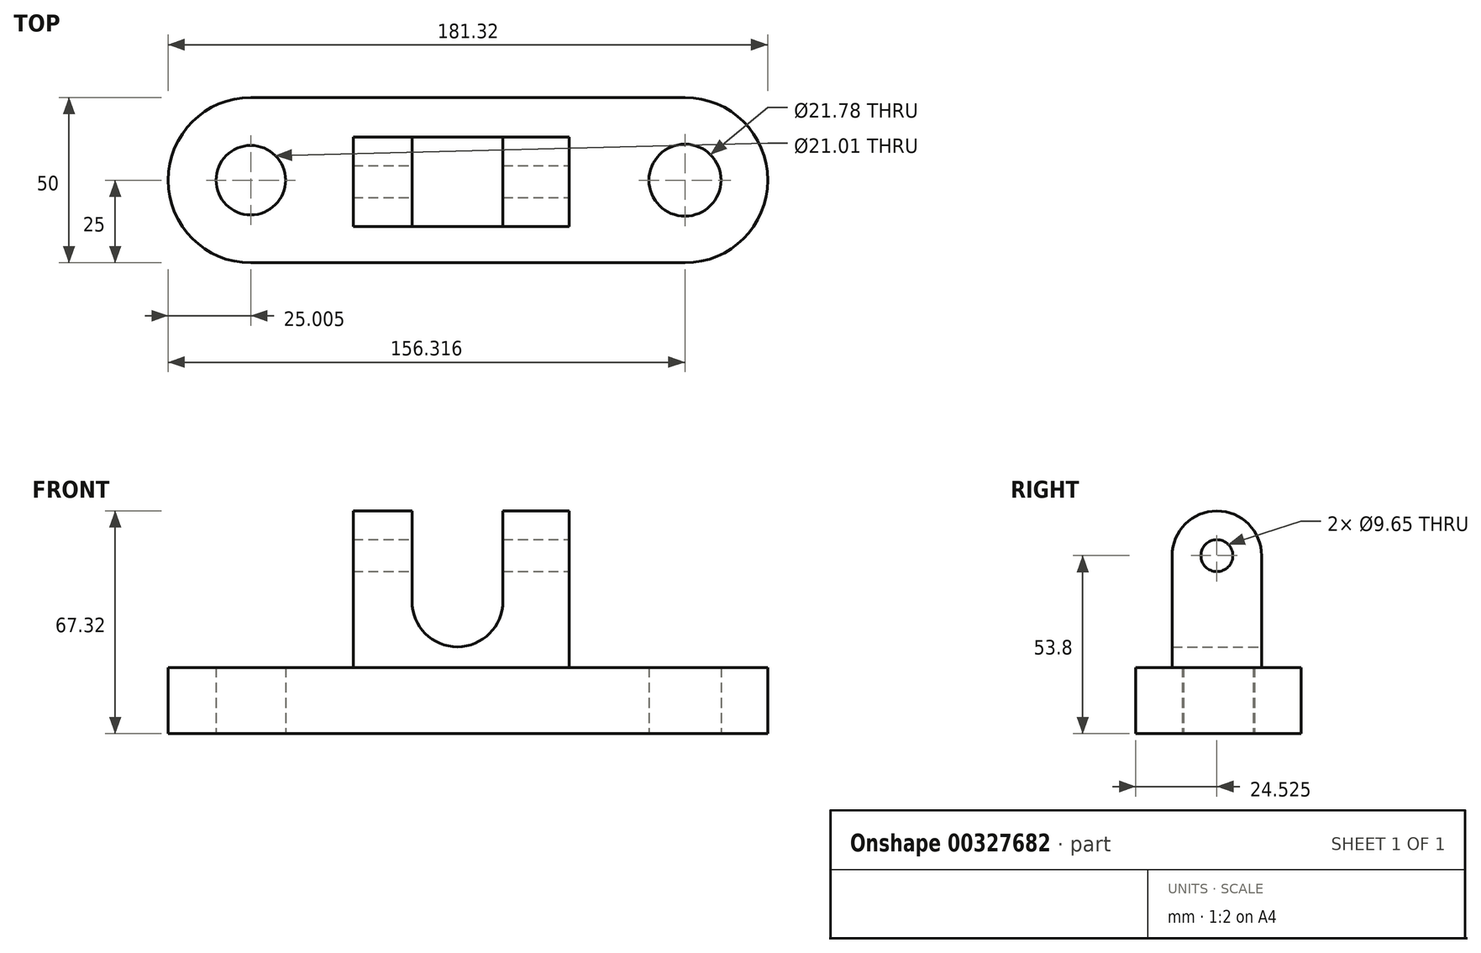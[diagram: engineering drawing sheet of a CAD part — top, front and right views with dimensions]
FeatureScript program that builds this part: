
annotation { "Feature Type Name" : "Feature", "Feature Type Description" : "" }
export const myFeature = defineFeature(function(context is Context, id is Id, definition is map)
    precondition{}
    {
        {
            var Q0;
            Q0=qCreatedBy(makeId("Top.planeOp"),FACE);
            var sketch = newSketch(context, id + "F0", { "sketchPlane" : qUnion([Q0])});
            skLineSegment(sketch, "E0", {"start": v(-77.75, 0) * mm, "end": v(53.57, 0) * mm});
            skArc(sketch, "E1.0.startCap", {"start": v(-77.75, -25) * mm, "mid": v(-102.75, 0) * mm, "end": v(-77.75, 25) * mm});
            skArc(sketch, "E1.0.endCap", {"start": v(53.57, 25) * mm, "mid": v(78.57, 0) * mm, "end": v(53.57, -25) * mm});
            skLineSegment(sketch, "E1.0.left", {"start": v(-77.75, 25) * mm, "end": v(53.57, 25) * mm});
            skLineSegment(sketch, "E1.0.right", {"start": v(-77.75, -25) * mm, "end": v(53.57, -25) * mm});
            skCircle(sketch, "E2", {"center": v(-77.75, 0) * mm, "radius": 10.5 * mm});
            skCircle(sketch, "E3", {"center": v(53.57, 0) * mm, "radius": 10.9 * mm});
            skSolve(sketch);
        }
        {
            var Q0;
            Q0 = qSketchRegion(id + "F0", true);
            extrude(context, id + "F1", {"entities" : qUnion([Q0]), "depth" : 20 * mm});
        }
        {
            var Q0;
            Q0=makeQuery(id+"F1.opExtrude","CAP_FACE",FACE,{"disambiguationData":[OSD([sQuery(id+"F0.wireOp",EDGE,"E1.0.startCap"),sQuery(id+"F0.wireOp",EDGE,"E1.0.endCap"),sQuery(id+"F0.wireOp",EDGE,"E1.0.left"),sQuery(id+"F0.wireOp",EDGE,"E1.0.right"),sQuery(id+"F0.wireOp",EDGE,"E2"),sQuery(id+"F0.wireOp",EDGE,"E3")])],"isStart":false});
            var sketch = newSketch(context, id + "F2", { "sketchPlane" : qUnion([Q0])});
            skLineSegment(sketch, "E4.bottom", {"start": v(18.48, -14) * mm, "end": v(-46.79, -14) * mm});
            skLineSegment(sketch, "E4.top", {"start": v(18.48, 13.04) * mm, "end": v(-46.79, 13.04) * mm});
            skLineSegment(sketch, "E4.left", {"start": v(18.48, -14) * mm, "end": v(18.48, 13.04) * mm});
            skLineSegment(sketch, "E4.right", {"start": v(-46.79, -14) * mm, "end": v(-46.79, 13.04) * mm});
            skSolve(sketch);
        }
        {
            var Q0;
            Q0 = qSketchRegion(id + "F2", true);
            extrude(context, id + "F3", {"entities" : qUnion([Q0]), "operationType" : NewBodyOperationType.ADD, "depth" : 33.8 * mm});
        }
        {
            var Q0;
            Q0=makeQuery(id+"F3.opExtrude","SWEPT_FACE",FACE,{"disambiguationData":[OSD([sQuery(id+"F2.wireOp",EDGE,"E4.left")])]});
            var sketch = newSketch(context, id + "F4", { "sketchPlane" : qUnion([Q0])});
            skArc(sketch, "E5", {"start": v(13.04, 53.8) * mm, "mid": v(-0.48, 67.32) * mm, "end": v(-14, 53.8) * mm});
            skLineSegment(sketch, "E6", {"start": v(-14, 53.8) * mm, "end": v(13.04, 53.8) * mm});
            skSolve(sketch);
        }
        {
            var Q0;
            Q0 = qSketchRegion(id + "F4", true);
            var Q1;
            Q1=makeQuery(id+"F3.opExtrude","SWEPT_FACE",FACE,{"disambiguationData":[OSD([sQuery(id+"F2.wireOp",EDGE,"E4.right")])]});
            extrude(context, id + "F5", {"entities" : qUnion([Q0]), "operationType" : NewBodyOperationType.ADD, "endBound" : BoundingType.UP_TO_SURFACE, "oppositeDirection" : true, "endBoundEntityFace" : qUnion([Q1]), "depth" : 25 * mm});
        }
        {
            var Q0;
            Q0=makeQuery(id+"F5.boolean.opBoolean","MERGE",FACE,{"derivedFrom":[makeQuery(id+"F3.opExtrude","SWEPT_FACE",FACE,{"disambiguationData":[OSD([sQuery(id+"F2.wireOp",EDGE,"E4.left")])]}),makeQuery(id+"F5.opExtrude","CAP_FACE",FACE,{"disambiguationData":[OSD([sQuery(id+"F4.wireOp",EDGE,"E5"),sQuery(id+"F4.wireOp",EDGE,"E6")])],"isStart":true})]});
            var sketch = newSketch(context, id + "F6", { "sketchPlane" : qUnion([Q0])});
            skCircle(sketch, "E7", {"center": v(-0.48, 53.8) * mm, "radius": 4.82 * mm});
            skSolve(sketch);
        }
        {
            var Q0;
            Q0 = qSketchRegion(id + "F6", true);
            extrude(context, id + "F7", {"entities" : qUnion([Q0]), "operationType" : NewBodyOperationType.REMOVE, "endBound" : BoundingType.THROUGH_ALL, "oppositeDirection" : true, "depth" : 25 * mm});
        }
        {
            var Q0;
            Q0=makeQuery(id+"F3.opExtrude","SWEPT_FACE",FACE,{"disambiguationData":[OSD([sQuery(id+"F2.wireOp",EDGE,"E4.top")])]});
            var sketch = newSketch(context, id + "F8", { "sketchPlane" : qUnion([Q0])});
            skLineSegment(sketch, "E8.bottom", {"start": v(1.52, 71.84) * mm, "end": v(28.99, 71.84) * mm});
            skLineSegment(sketch, "E8.left", {"start": v(1.52, 71.84) * mm, "end": v(1.52, 39.96) * mm});
            skLineSegment(sketch, "E8.right", {"start": v(28.99, 71.84) * mm, "end": v(28.99, 39.96) * mm});
            skArc(sketch, "E9", {"start": v(1.52, 39.96) * mm, "mid": v(15.25, 26.23) * mm, "end": v(28.99, 39.96) * mm});
            skSolve(sketch);
        }
        {
            var Q0;
            Q0 = qSketchRegion(id + "F8", true);
            extrude(context, id + "F9", {"entities" : qUnion([Q0]), "operationType" : NewBodyOperationType.REMOVE, "endBound" : BoundingType.THROUGH_ALL, "oppositeDirection" : true, "depth" : 25 * mm});
        }
    });
